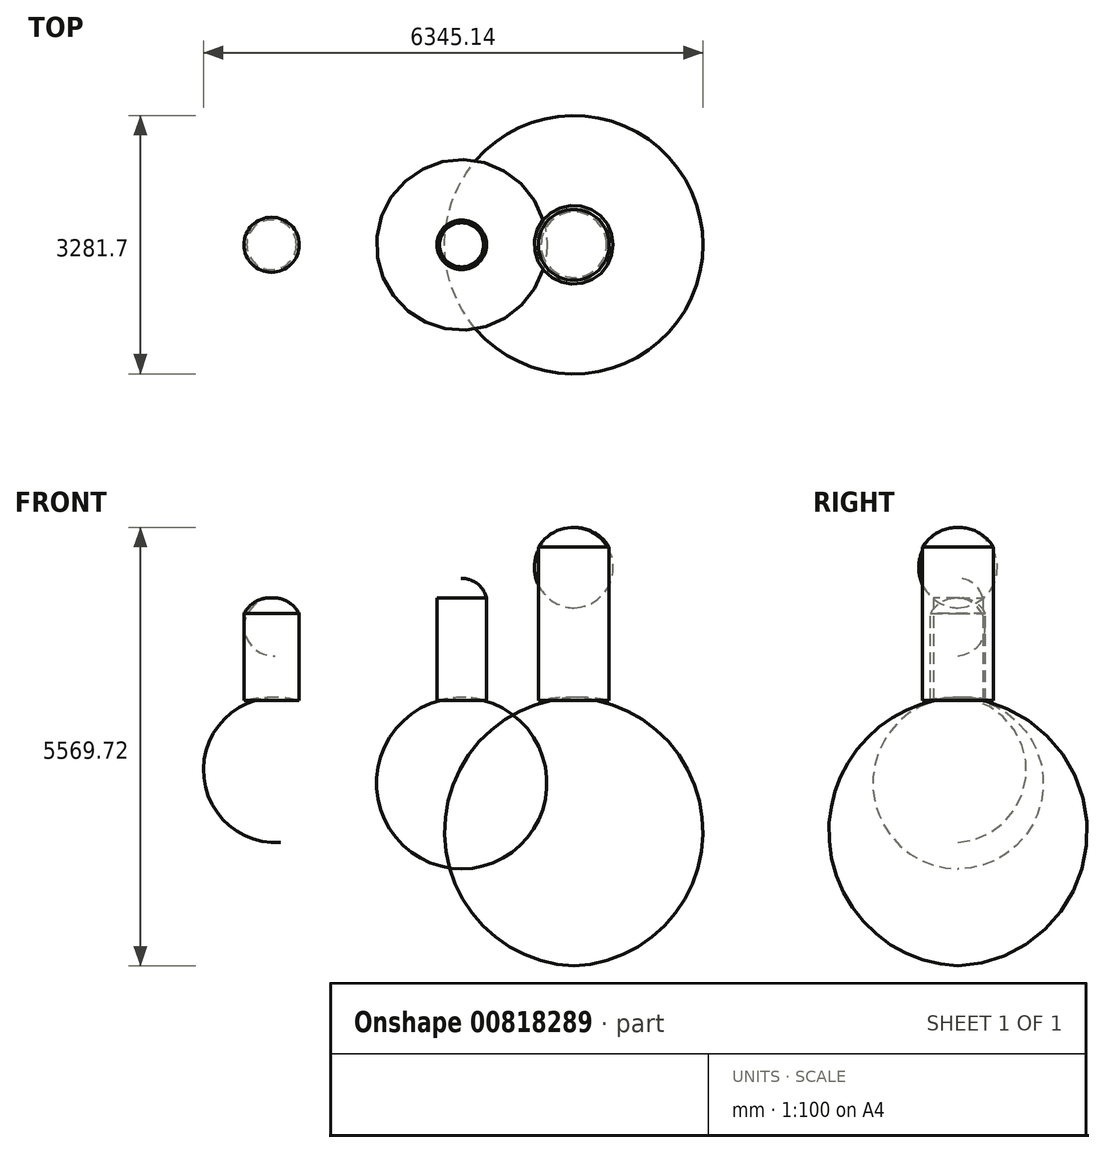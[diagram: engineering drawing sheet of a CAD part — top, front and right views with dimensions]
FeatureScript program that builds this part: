
annotation { "Feature Type Name" : "Feature", "Feature Type Description" : "" }
export const myFeature = defineFeature(function(context is Context, id is Id, definition is map)
    precondition{}
    {
        {
            var Q0;
            Q0=qCreatedBy(makeId("Front.planeOp"),FACE);
            var sketch = newSketch(context, id + "F0", { "sketchPlane" : qUnion([Q0])});
            skLineSegment(sketch, "E0", {"start": v(0, 0) * mm, "end": v(350, 0) * mm, "construction": true});
            skLineSegment(sketch, "E1", {"start": v(0, 0) * mm, "end": v(0, 1300) * mm, "construction": true});
            skLineSegment(sketch, "E2", {"start": v(350, 0) * mm, "end": v(350, 1100) * mm});
            skArc(sketch, "E3", {"start": v(350, 1100) * mm, "mid": v(204.8, 1252.14) * mm, "end": v(0, 1300) * mm});
            skArc(sketch, "E4", {"start": v(315, 0) * mm, "mid": v(159.01, 31.12) * mm, "end": v(0, 35) * mm});
            skLineSegment(sketch, "E5", {"start": v(315, 0) * mm, "end": v(350, 0) * mm});
            skLineSegment(sketch, "E6", {"start": v(0, 1300) * mm, "end": v(0, 35) * mm});
            skSolve(sketch);
        }
        {
            var Q0;
            Q0 = qSketchRegion(id + "F0", true);
            var Q1;
            Q1=sQuery(id+"F0.wireOp",EDGE,"E6");
            revolve(context, id + "F1", {"surfaceOperationType" : NewSurfaceOperationType.NEW, "entities" : qUnion([Q0]), "axis" : qUnion([Q1]), "revolveType" : RevolveType.FULL});
        }
        {
            var Q0;
            Q0=qCreatedBy(makeId("Front.planeOp"),FACE);
            var sketch = newSketch(context, id + "F2", { "sketchPlane" : qUnion([Q0])});
            skLineSegment(sketch, "E7", {"start": v(2414.68, 0) * mm, "end": v(2414.68, 1550) * mm, "construction": true});
            skLineSegment(sketch, "E8", {"start": v(2414.68, 0) * mm, "end": v(2729.68, 0) * mm, "construction": true});
            skArc(sketch, "E9", {"start": v(2694.68, 0) * mm, "mid": v(2555.82, 26.6) * mm, "end": v(2414.68, 35) * mm});
            skLineSegment(sketch, "E10", {"start": v(2729.68, 0) * mm, "end": v(2729.68, 1300) * mm});
            skArc(sketch, "E11", {"start": v(2729.68, 1300) * mm, "mid": v(2614.9, 1478.84) * mm, "end": v(2414.68, 1550) * mm});
            skLineSegment(sketch, "E12", {"start": v(2694.68, 0) * mm, "end": v(2729.68, 0) * mm});
            skLineSegment(sketch, "E13", {"start": v(2414.68, 35) * mm, "end": v(2414.68, 1550) * mm});
            skSolve(sketch);
        }
        {
            var Q0;
            Q0 = qSketchRegion(id + "F2", true);
            var Q1;
            Q1=sQuery(id+"F2.wireOp",EDGE,"E13");
            revolve(context, id + "F3", {"surfaceOperationType" : NewSurfaceOperationType.NEW, "entities" : qUnion([Q0]), "axis" : qUnion([Q1]), "revolveType" : RevolveType.FULL});
        }
        {
            var Q0;
            Q0=qCreatedBy(makeId("Front.planeOp"),FACE);
            var sketch = newSketch(context, id + "F4", { "sketchPlane" : qUnion([Q0])});
            skLineSegment(sketch, "E14", {"start": v(3388.5, 0) * mm, "end": v(3838.5, 0) * mm, "construction": true});
            skLineSegment(sketch, "E15", {"start": v(3838.5, 35) * mm, "end": v(3838.5, 2195) * mm});
            skArc(sketch, "E16", {"start": v(3838.5, 35) * mm, "mid": v(3629.92, 30.21) * mm, "end": v(3423.5, 0) * mm});
            skLineSegment(sketch, "E17", {"start": v(3423.5, 0) * mm, "end": v(3388.5, 0) * mm});
            skLineSegment(sketch, "E18", {"start": v(3388.5, 0) * mm, "end": v(3388.5, 1945) * mm});
            skArc(sketch, "E19", {"start": v(3838.5, 2195) * mm, "mid": v(3579.7, 2130.83) * mm, "end": v(3388.5, 1945) * mm});
            skSolve(sketch);
        }
        {
            var Q0;
            Q0 = qSketchRegion(id + "F4", true);
            var Q1;
            Q1=sQuery(id+"F4.wireOp",EDGE,"E15");
            revolve(context, id + "F5", {"surfaceOperationType" : NewSurfaceOperationType.NEW, "entities" : qUnion([Q0]), "axis" : qUnion([Q1]), "revolveType" : RevolveType.FULL});
        }
    });
